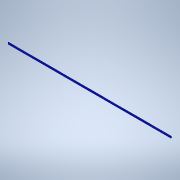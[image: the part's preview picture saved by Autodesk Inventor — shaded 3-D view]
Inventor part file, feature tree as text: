
AUTODESK INVENTOR PART (.ipt)
format: ipt  version: 2020.3 (Build 243373000, 373)  size: 872,448 bytes
history: native  units: mm (DEFAULTED — no unit token found)
features: extrude x2, sketch x2, pattern_linear x1
ambient origin geometry x8: Origin, YZ Plane, XZ Plane, XY Plane, X Axis, Y Axis, Z Axis, Center Point
bodies: Solid1 (feature_tree)
feature tree (5):
  extrude  "Extrusion1"  Depth=5.0mm TaperAngle=0.0deg
  extrude  "Extrusion2"  [1 undecoded]
  pattern_linear  "Rectangular Pattern1"  [2 undecoded]
  sketch  "Sketch_1"  dims[d0=865.0mm d1=0.0mm d2=5.0mm d3=0.0mm]
  sketch  "Sketch_5"  dims[d4=6410.0mm d6=3.14159mm d7=10.0mm d9=0.0mm]
note: 3 required parameter values undecoded (feature->parameter linkage not recoverable at this tier; creation-order binding heuristic only, values carry confidence <= 0.55)
